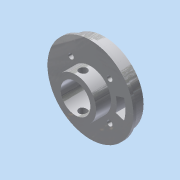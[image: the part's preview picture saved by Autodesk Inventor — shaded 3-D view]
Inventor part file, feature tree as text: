
AUTODESK INVENTOR PART (.ipt)
format: ipt  version: 2015 (Build 190159000, 159)  size: 192,000 bytes
history: native  units: in
note: dims shown in document units (in); Inventor stores cm internally (conversion verified against a paired STEP export)
features: other x4, extrude x4, sketch x4
ambient origin geometry x8: Origin, YZ Plane, XZ Plane, XY Plane, X Axis, Y Axis, Z Axis, Center Point
bodies: Solid1 (feature_tree)
feature tree (12):
  other  "StatorCore.ipt"
  extrude  "Extrusion1"  Depth=0.3937in
  extrude  "Extrusion2"  Depth=0.3543in
  extrude  "Extrusion3"  Depth=0.201in
  extrude  "Extrusion4"  Depth=0.375in TaperAngle=0.0deg
  other  "TaggingFeature1"
  sketch  "Sketch1"  dims[d0=0.3937in d1=0.748in]
  sketch  "Sketch2"  dims[d2=0.3543in d3=0.0in d4=0.25in]
  sketch  "Sketch3"  dims[d5=0.375in d6=0.0in d7=0.201in]
  sketch  "Sketch4"  dims[d8=0.1875in d9=0.375in d10=0.0in d11=1.9685in d12=2.1654in d13=0.0787in d14=0.0in]
  other  "Solid1::StatorCore.ipt"
  other  "Srf1"
